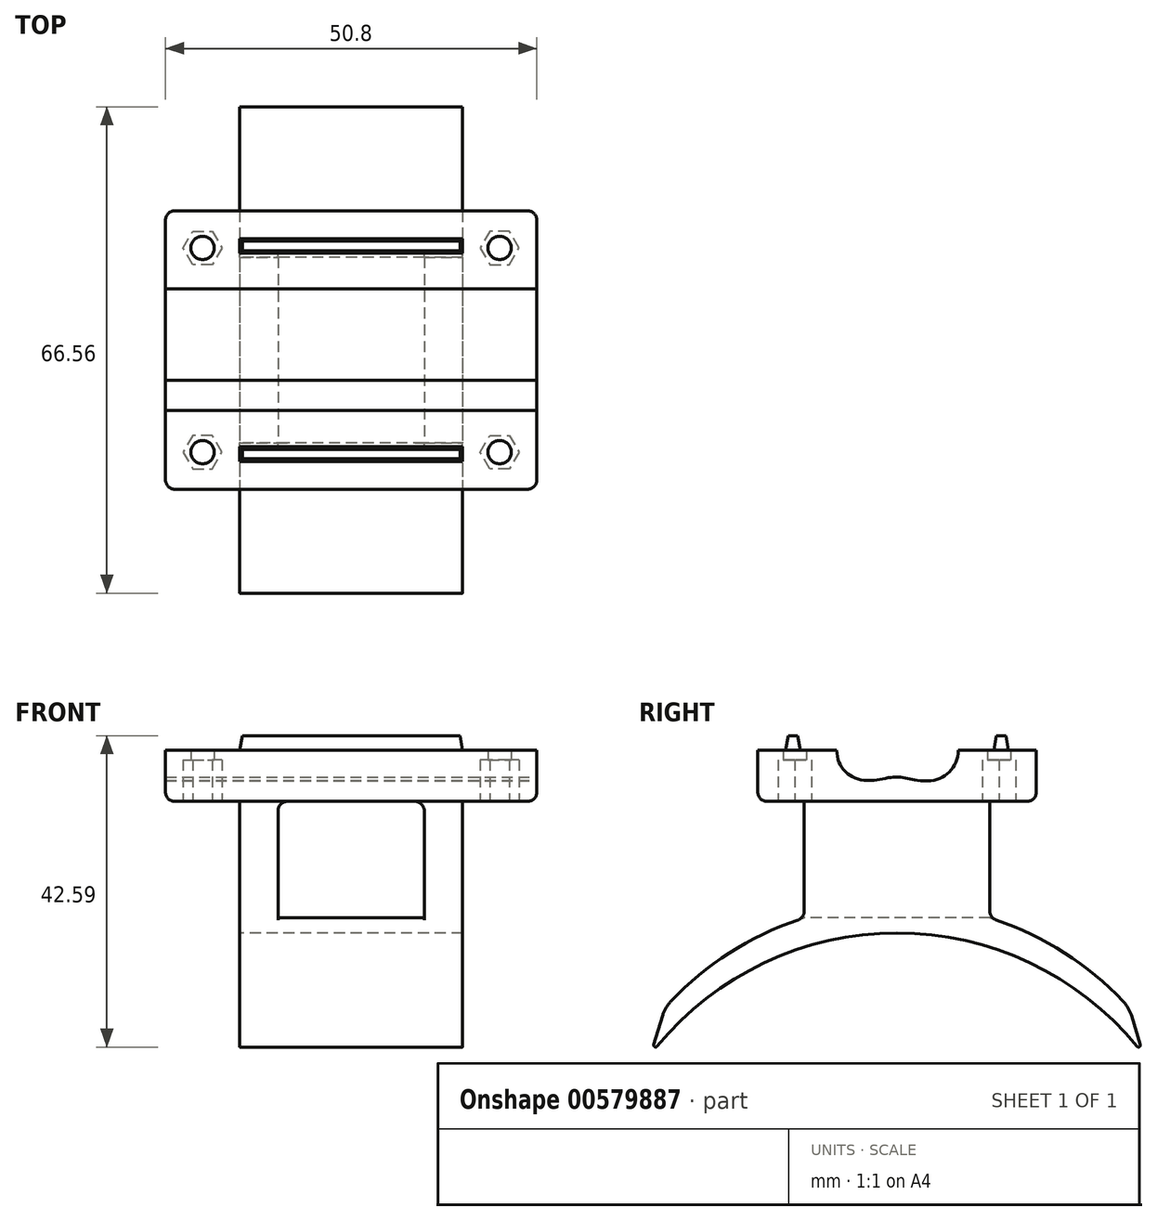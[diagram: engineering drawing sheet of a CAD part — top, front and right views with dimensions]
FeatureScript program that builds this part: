
annotation { "Feature Type Name" : "Feature", "Feature Type Description" : "" }
export const myFeature = defineFeature(function(context is Context, id is Id, definition is map)
    precondition{}
    {
        {
            var Q0;
            Q0=qCreatedBy(makeId("Top.planeOp"),FACE);
            var sketch = newSketch(context, id + "F0", { "sketchPlane" : qUnion([Q0])});
            skLineSegment(sketch, "E0.bottom", {"start": v(-38.1, 0) * mm, "end": v(38.1, 0) * mm});
            skLineSegment(sketch, "E0.top", {"start": v(-38.1, -4.13) * mm, "end": v(38.1, -4.13) * mm});
            skLineSegment(sketch, "E0.left", {"start": v(-38.1, 0) * mm, "end": v(-38.1, -4.13) * mm});
            skLineSegment(sketch, "E0.right", {"start": v(38.1, 0) * mm, "end": v(38.1, -4.13) * mm});
            skLineSegment(sketch, "E1.top", {"start": v(-38.1, 4.2) * mm, "end": v(38.1, 4.2) * mm});
            skLineSegment(sketch, "E1.left", {"start": v(-38.1, 0) * mm, "end": v(-38.1, 4.2) * mm});
            skLineSegment(sketch, "E1.right", {"start": v(38.1, 0) * mm, "end": v(38.1, 4.2) * mm});
            skLineSegment(sketch, "E2.MirrorCS", {"start": v(38.1, 8.38) * mm, "end": v(38.1, 4.2) * mm});
            skLineSegment(sketch, "E3.MirrorCS", {"start": v(-38.1, 8.38) * mm, "end": v(38.1, 8.38) * mm});
            skLineSegment(sketch, "E4.MirrorCS", {"start": v(-38.1, 8.38) * mm, "end": v(-38.1, 4.2) * mm});
            skLineSegment(sketch, "E5.MirrorCS", {"start": v(38.1, -8.25) * mm, "end": v(38.1, -4.12) * mm});
            skLineSegment(sketch, "E6.MirrorCS", {"start": v(-38.1, -8.25) * mm, "end": v(38.1, -8.25) * mm});
            skLineSegment(sketch, "E7.MirrorCS", {"start": v(-38.1, -8.25) * mm, "end": v(-38.1, -4.12) * mm});
            skSolve(sketch);
        }
        {
            var Q0;
            Q0=qCreatedBy(makeId("Top.planeOp"),FACE);
            var sketch = newSketch(context, id + "F1", { "sketchPlane" : qUnion([Q0])});
            skLineSegment(sketch, "E8.bottom", {"start": v(-25.4, 19.05) * mm, "end": v(25.4, 19.05) * mm});
            skLineSegment(sketch, "E8.top", {"start": v(-25.4, -19.05) * mm, "end": v(25.4, -19.05) * mm});
            skLineSegment(sketch, "E8.left", {"start": v(-25.4, 19.05) * mm, "end": v(-25.4, -19.05) * mm});
            skLineSegment(sketch, "E8.right", {"start": v(25.4, 19.05) * mm, "end": v(25.4, -19.05) * mm});
            skSolve(sketch);
        }
        {
            var Q0;
            Q0=qSketchRegion(id+"F1",true);
            extrude(context, id + "F2", {"entities" : qUnion([Q0]), "oppositeDirection" : true, "depth" : 7 * mm, "offsetDistance" : 25.4 * mm});
        }
        {
            var Q0;
            Q0=makeQuery(id+"F2.opExtrude","SWEPT_FACE",FACE,{"disambiguationData":[OSD([sQuery(id+"F1.wireOp",EDGE,"E8.right")])]});
            var sketch = newSketch(context, id + "F3", { "sketchPlane" : qUnion([Q0])});
            skLineSegment(sketch, "E9.0", {"start": v(-8.25, 0) * mm, "end": v(-4.12, 0) * mm});
            skLineSegment(sketch, "E10.0", {"start": v(8.38, 0) * mm, "end": v(4.2, 0) * mm});
            skArc(sketch, "E11", {"start": v(-4.13, 4.13) * mm, "mid": v(-8.25, 0) * mm, "end": v(-4.12, -4.13) * mm});
            skArc(sketch, "E12", {"start": v(4.2, -4.2) * mm, "mid": v(8.38, 0) * mm, "end": v(4.2, 4.2) * mm});
            skFitSpline(sketch, "E13", {"points": [v(-4.12, 4.13) * mm, v(0, 3.54) * mm, v(4.2, 4.2) * mm], "startDerivative": vector(10.24, -0.07) * mm, "endDerivative": vector(9.95, 0.46) * mm});
            skFitSpline(sketch, "E14", {"points": [v(-4.12, -4.13) * mm, v(0, -3.63) * mm, v(4.2, -4.2) * mm], "startDerivative": vector(7.18, -0.46) * mm, "endDerivative": vector(12.23, 0.06) * mm});
            skSolve(sketch);
        }
        {
            var Q0;
            Q0=qSketchRegion(id+"F3",true);
            var Q1;
            Q1=makeQuery(id+"F2.opExtrude","SWEPT_FACE",FACE,{"disambiguationData":[OSD([sQuery(id+"F1.wireOp",EDGE,"E8.left")])]});
            extrude(context, id + "F4", {"entities" : qUnion([Q0]), "operationType" : NewBodyOperationType.REMOVE, "endBound" : BoundingType.UP_TO_SURFACE, "oppositeDirection" : true, "depth" : 25.4 * mm, "endBoundEntityFace" : qUnion([Q1]), "offsetDistance" : 25.4 * mm});
        }
        {
            var Q0;
            Q0=qCreatedBy(makeId("Right.planeOp"),FACE);
            var sketch = newSketch(context, id + "F5", { "sketchPlane" : qUnion([Q0])});
            skArc(sketch, "E15", {"start": v(33.66, -41.53) * mm, "mid": v(0, -24.98) * mm, "end": v(-33.65, -41.53) * mm});
            skArc(sketch, "E16", {"start": v(31.75, -35.23) * mm, "mid": v(0, -20.98) * mm, "end": v(-31.75, -35.23) * mm});
            skLineSegment(sketch, "E17.0", {"start": v(19.05, -6.99) * mm, "end": v(-19.05, -6.99) * mm});
            skLineSegment(sketch, "E18", {"start": v(12.7, -22.93) * mm, "end": v(12.7, -6.99) * mm});
            skLineSegment(sketch, "E19", {"start": v(12.7, -6.99) * mm, "end": v(-12.7, -6.99) * mm});
            skLineSegment(sketch, "E20", {"start": v(-12.7, -6.99) * mm, "end": v(-12.7, -22.93) * mm});
            skLineSegment(sketch, "E21", {"start": v(-33.65, -41.53) * mm, "end": v(-31.75, -35.23) * mm});
            skLineSegment(sketch, "E22", {"start": v(31.75, -35.23) * mm, "end": v(33.66, -41.53) * mm});
            skSolve(sketch);
        }
        {
            var Q0;
            Q0=qSketchRegion(id+"F5",true);
            extrude(context, id + "F6", {"entities" : qUnion([Q0]), "operationType" : NewBodyOperationType.ADD, "depth" : 15.24 * mm, "offsetDistance" : 25.4 * mm, "hasSecondDirection" : true, "secondDirectionOppositeDirection" : true, "secondDirectionDepth" : 15.24 * mm});
        }
        {
            var Q0;
            Q0=makeQuery(id+"F6.opExtrude","SWEPT_FACE",FACE,{"disambiguationData":[OSD([sQuery(id+"F5.wireOp",EDGE,"E20")])]});
            var sketch = newSketch(context, id + "F7", { "sketchPlane" : qUnion([Q0])});
            skLineSegment(sketch, "E23.bottom", {"start": v(-10, -6.99) * mm, "end": v(10, -6.99) * mm});
            skLineSegment(sketch, "E23.top", {"start": v(-10, -22.93) * mm, "end": v(10, -22.93) * mm});
            skLineSegment(sketch, "E23.left", {"start": v(-10, -6.99) * mm, "end": v(-10, -22.93) * mm});
            skLineSegment(sketch, "E23.right", {"start": v(10, -6.98) * mm, "end": v(10, -22.93) * mm});
            skSolve(sketch);
        }
        {
            var Q0;
            Q0=qSketchRegion(id+"F7",true);
            extrude(context, id + "F8", {"entities" : qUnion([Q0]), "operationType" : NewBodyOperationType.REMOVE, "oppositeDirection" : true, "depth" : 25.4 * mm, "offsetDistance" : 25.4 * mm});
        }
        {
            var Q0;
            Q0=makeQuery(id+"F8.boolean.opBoolean","MERGE",FACE,{"derivedFrom":[makeQuery(id+"F2.opExtrude","CAP_FACE",FACE,{"disambiguationData":[OSD([sQuery(id+"F1.wireOp",EDGE,"E8.bottom"),sQuery(id+"F1.wireOp",EDGE,"E8.top"),sQuery(id+"F1.wireOp",EDGE,"E8.left"),sQuery(id+"F1.wireOp",EDGE,"E8.right")])],"isStart":false}),makeQuery(id+"F8.opExtrude","SWEPT_FACE",FACE,{"disambiguationData":[OSD([sQuery(id+"F7.wireOp",EDGE,"E23.bottom")])]})]});
            var sketch = newSketch(context, id + "F9", { "sketchPlane" : qUnion([Q0])});
            skCircle(sketch, "E24", {"center": v(20.32, -13.97) * mm, "radius": 1.6 * mm});
            skCircle(sketch, "E25.MirrorC", {"center": v(-20.32, -13.97) * mm, "radius": 1.6 * mm});
            skCircle(sketch, "E26.MirrorC", {"center": v(-20.32, 13.97) * mm, "radius": 1.6 * mm});
            skCircle(sketch, "E27.MirrorC", {"center": v(20.32, 13.97) * mm, "radius": 1.6 * mm});
            skSolve(sketch);
        }
        {
            var Q0;
            Q0=qSketchRegion(id+"F9",true);
            extrude(context, id + "F10", {"entities" : qUnion([Q0]), "operationType" : NewBodyOperationType.REMOVE, "oppositeDirection" : true, "depth" : 25.4 * mm, "offsetDistance" : 25.4 * mm});
        }
        {
            var Q0;
            Q0=makeQuery(id+"F8.boolean.opBoolean","MERGE",FACE,{"derivedFrom":[makeQuery(id+"F2.opExtrude","CAP_FACE",FACE,{"disambiguationData":[OSD([sQuery(id+"F1.wireOp",EDGE,"E8.bottom"),sQuery(id+"F1.wireOp",EDGE,"E8.top"),sQuery(id+"F1.wireOp",EDGE,"E8.left"),sQuery(id+"F1.wireOp",EDGE,"E8.right")])],"isStart":false}),makeQuery(id+"F8.opExtrude","SWEPT_FACE",FACE,{"disambiguationData":[OSD([sQuery(id+"F7.wireOp",EDGE,"E23.bottom")])]})]});
            var sketch = newSketch(context, id + "F11", { "sketchPlane" : qUnion([Q0])});
            skCircle(sketch, "E28.0", {"center": v(20.32, -13.97) * mm, "radius": 1.6 * mm});
            skCircle(sketch, "E29.cCircle", {"center": v(20.32, -13.97) * mm, "radius": 2.65 * mm, "construction": true});
            skLineSegment(sketch, "E29.0", {"start": v(22.97, -13.97) * mm, "end": v(21.64, -16.26) * mm});
            skLineSegment(sketch, "E29.1", {"start": v(21.65, -16.26) * mm, "end": v(19, -16.26) * mm});
            skLineSegment(sketch, "E29.2", {"start": v(19, -16.26) * mm, "end": v(17.67, -13.97) * mm});
            skLineSegment(sketch, "E29.3", {"start": v(17.67, -13.97) * mm, "end": v(19, -11.68) * mm});
            skLineSegment(sketch, "E29.4", {"start": v(19, -11.68) * mm, "end": v(21.65, -11.68) * mm});
            skLineSegment(sketch, "E29.5", {"start": v(21.65, -11.68) * mm, "end": v(22.97, -13.97) * mm});
            skLineSegment(sketch, "E30.MirrorCS", {"start": v(-21.65, -11.68) * mm, "end": v(-22.97, -13.97) * mm});
            skLineSegment(sketch, "E31.MirrorCS", {"start": v(-17.67, -13.97) * mm, "end": v(-19, -11.68) * mm});
            skLineSegment(sketch, "E32.MirrorCS", {"start": v(-22.97, -13.97) * mm, "end": v(-21.64, -16.26) * mm});
            skLineSegment(sketch, "E33.MirrorCS", {"start": v(-19, -16.26) * mm, "end": v(-17.67, -13.97) * mm});
            skCircle(sketch, "E34.MirrorC", {"center": v(-20.32, -13.97) * mm, "radius": 1.6 * mm});
            skLineSegment(sketch, "E35.MirrorCS", {"start": v(-19, -11.68) * mm, "end": v(-21.65, -11.68) * mm});
            skLineSegment(sketch, "E36.MirrorCS", {"start": v(-21.65, -16.26) * mm, "end": v(-19, -16.26) * mm});
            skCircle(sketch, "E37.MirrorC", {"center": v(-20.32, -13.97) * mm, "radius": 2.65 * mm, "construction": true});
            skLineSegment(sketch, "E38.MirrorCS", {"start": v(-17.67, 13.97) * mm, "end": v(-19, 11.68) * mm});
            skLineSegment(sketch, "E39.MirrorCS", {"start": v(-19, 16.26) * mm, "end": v(-17.67, 13.97) * mm});
            skLineSegment(sketch, "E40.MirrorCS", {"start": v(21.65, 11.68) * mm, "end": v(22.97, 13.97) * mm});
            skLineSegment(sketch, "E41.MirrorCS", {"start": v(-21.65, 16.26) * mm, "end": v(-19, 16.26) * mm});
            skCircle(sketch, "E42.MirrorC", {"center": v(-20.32, 13.97) * mm, "radius": 1.6 * mm});
            skLineSegment(sketch, "E43.MirrorCS", {"start": v(-22.97, 13.97) * mm, "end": v(-21.64, 16.26) * mm});
            skLineSegment(sketch, "E44.MirrorCS", {"start": v(17.67, 13.97) * mm, "end": v(19, 11.68) * mm});
            skLineSegment(sketch, "E45.MirrorCS", {"start": v(-21.65, 11.68) * mm, "end": v(-22.97, 13.97) * mm});
            skLineSegment(sketch, "E46.MirrorCS", {"start": v(-19, 11.68) * mm, "end": v(-21.65, 11.68) * mm});
            skLineSegment(sketch, "E47.MirrorCS", {"start": v(22.97, 13.97) * mm, "end": v(21.64, 16.26) * mm});
            skLineSegment(sketch, "E48.MirrorCS", {"start": v(19, 16.26) * mm, "end": v(17.67, 13.97) * mm});
            skLineSegment(sketch, "E49.MirrorCS", {"start": v(21.65, 16.26) * mm, "end": v(19, 16.26) * mm});
            skLineSegment(sketch, "E50.MirrorCS", {"start": v(19, 11.68) * mm, "end": v(21.65, 11.68) * mm});
            skCircle(sketch, "E51.MirrorC", {"center": v(20.32, 13.97) * mm, "radius": 2.65 * mm, "construction": true});
            skCircle(sketch, "E52.MirrorC", {"center": v(20.32, 13.97) * mm, "radius": 1.6 * mm});
            skCircle(sketch, "E53.MirrorC", {"center": v(-20.32, 13.97) * mm, "radius": 2.65 * mm, "construction": true});
            skSolve(sketch);
        }
        {
            var Q0;
            Q0=qSketchRegion(id+"F11",true);
            extrude(context, id + "F12", {"entities" : qUnion([Q0]), "operationType" : NewBodyOperationType.REMOVE, "oppositeDirection" : true, "depth" : 5.7 * mm, "offsetDistance" : 25.4 * mm});
        }
        {
            var Q0;
            {var subQ0=sQuery(id+"F1.wireOp",EDGE,"E8.bottom");var subQ1=sQuery(id+"F1.wireOp",EDGE,"E8.right");var subQ2=sQuery(id+"F1.wireOp",EDGE,"E8.left");Q0=makeQuery(id+"F4.boolean.opBoolean","SPLIT",FACE,{"disambiguationData":[TD([makeQuery(id+"F2.opExtrude","SWEPT_FACE",FACE,{"disambiguationData":[OSD([subQ0])]})])],"derivedFrom":makeQuery(id+"F2.opExtrude","CAP_FACE",FACE,{"disambiguationData":[OSD([subQ0,sQuery(id+"F1.wireOp",EDGE,"E8.top"),subQ2,subQ1])],"isStart":true})});}
            var sketch = newSketch(context, id + "F13", { "sketchPlane" : qUnion([Q0])});
            skLineSegment(sketch, "E54.bottom", {"start": v(-15.24, 15.24) * mm, "end": v(15.24, 15.24) * mm});
            skLineSegment(sketch, "E54.top", {"start": v(-15.24, 13.24) * mm, "end": v(15.24, 13.24) * mm});
            skLineSegment(sketch, "E54.left", {"start": v(-15.24, 15.24) * mm, "end": v(-15.24, 13.24) * mm});
            skLineSegment(sketch, "E54.right", {"start": v(15.24, 15.24) * mm, "end": v(15.24, 13.24) * mm});
            skLineSegment(sketch, "E55.MirrorCS", {"start": v(-15.24, -15.24) * mm, "end": v(-15.24, -13.24) * mm});
            skLineSegment(sketch, "E56.MirrorCS", {"start": v(15.24, -15.24) * mm, "end": v(15.24, -13.24) * mm});
            skLineSegment(sketch, "E57.MirrorCS", {"start": v(-15.24, -15.24) * mm, "end": v(15.24, -15.24) * mm});
            skLineSegment(sketch, "E58.MirrorCS", {"start": v(-15.24, -13.24) * mm, "end": v(15.24, -13.24) * mm});
            skSolve(sketch);
        }
        {
            var Q0;
            Q0=qSketchRegion(id+"F13",true);
            extrude(context, id + "F14", {"entities" : qUnion([Q0]), "operationType" : NewBodyOperationType.ADD, "depth" : 2 * mm, "offsetDistance" : 25.4 * mm, "hasDraft" : true, "draftAngle" : 10 * degree, "draftPullDirection" : true});
        }
        {
            var Q0;
            Q0=makeQuery(id+"F6.opExtrude","SWEPT_EDGE",EDGE,{"disambiguationData":[OSD([sQuery(id+"F5.wireOp",EDGE,"E15"),sQuery(id+"F5.wireOp",EDGE,"E22")])]});
            var Q1;
            Q1=makeQuery(id+"F6.opExtrude","SWEPT_EDGE",EDGE,{"disambiguationData":[OSD([sQuery(id+"F5.wireOp",EDGE,"E15"),sQuery(id+"F5.wireOp",EDGE,"E21")])]});
            fillet(context, id + "F15", {"entities" : qUnion([Q0, Q1]), "radius" : 0.25 * mm, "tangentPropagation" : true, "allowEdgeOverflow" : false});
        }
        {
            var Q0;
            Q0=makeQuery(id+"F6.opExtrude","SWEPT_EDGE",EDGE,{"disambiguationData":[OSD([sQuery(id+"F5.wireOp",EDGE,"E16"),sQuery(id+"F5.wireOp",EDGE,"E22")])]});
            var Q1;
            Q1=makeQuery(id+"F6.opExtrude","SWEPT_EDGE",EDGE,{"disambiguationData":[OSD([sQuery(id+"F5.wireOp",EDGE,"E16"),sQuery(id+"F5.wireOp",EDGE,"E21")])]});
            fillet(context, id + "F16", {"entities" : qUnion([Q0, Q1]), "radius" : 5.08 * mm, "tangentPropagation" : true, "allowEdgeOverflow" : false});
        }
        {
            var Q0;
            {var subQ1=sQuery(id+"F5.wireOp",EDGE,"E16");var subQ2=sQuery(id+"F5.wireOp",EDGE,"E20");Q0=makeQuery(id+"F8.boolean.opBoolean","SPLIT",EDGE,{"disambiguationData":[TD([makeQuery(id+"F8.opExtrude","SWEPT_FACE",FACE,{"disambiguationData":[OSD([sQuery(id+"F7.wireOp",EDGE,"E23.right")])]})])],"derivedFrom":makeQuery(id+"F6.opExtrude","SWEPT_EDGE",EDGE,{"disambiguationData":[OSD([subQ1,subQ2])]})});}
            var Q1;
            {var subQ0=sQuery(id+"F5.wireOp",EDGE,"E20");var subQ2=sQuery(id+"F5.wireOp",EDGE,"E16");Q1=makeQuery(id+"F8.boolean.opBoolean","SPLIT",EDGE,{"disambiguationData":[TD([makeQuery(id+"F8.opExtrude","SWEPT_FACE",FACE,{"disambiguationData":[OSD([sQuery(id+"F7.wireOp",EDGE,"E23.left")])]})])],"derivedFrom":makeQuery(id+"F6.opExtrude","SWEPT_EDGE",EDGE,{"disambiguationData":[OSD([subQ2,subQ0])]})});}
            var Q2;
            {var subQ0=sQuery(id+"F5.wireOp",EDGE,"E18");var subQ1=makeQuery(id+"F6.opExtrude","SWEPT_FACE",FACE,{"disambiguationData":[OSD([subQ0])]});var subQ2=sQuery(id+"F5.wireOp",EDGE,"E22");var subQ3=sQuery(id+"F5.wireOp",EDGE,"E16");var subQ4=makeQuery(id+"F6.opExtrude","SWEPT_FACE",FACE,{"disambiguationData":[OSD([subQ3]),TDD([makeQuery(id+"F5.imprint","IMPRINT",EDGE,{"disambiguationData":[TD([[makeQuery(id+"F5.imprint","INTERSECT",VERTEX,{"derivedFrom":[subQ3,subQ2]}),-1.0]])],"derivedFrom":subQ3})])]});Q2=makeQuery(id+"F8.boolean.opBoolean","SPLIT",EDGE,{"disambiguationData":[topologyDisambiguationEdgeConnected([subQ4,subQ1]),TD([makeQuery(id+"F8.opExtrude","SWEPT_FACE",FACE,{"disambiguationData":[OSD([sQuery(id+"F7.wireOp",EDGE,"E23.right")])]})])],"derivedFrom":makeQuery(id+"F6.opExtrude","SWEPT_EDGE",EDGE,{"disambiguationData":[OSD([subQ3,subQ0])]})});}
            var Q3;
            {var subQ0=sQuery(id+"F5.wireOp",EDGE,"E18");var subQ1=makeQuery(id+"F6.opExtrude","SWEPT_FACE",FACE,{"disambiguationData":[OSD([subQ0])]});var subQ2=sQuery(id+"F5.wireOp",EDGE,"E22");var subQ3=sQuery(id+"F5.wireOp",EDGE,"E16");var subQ4=makeQuery(id+"F6.opExtrude","SWEPT_FACE",FACE,{"disambiguationData":[OSD([subQ3]),TDD([makeQuery(id+"F5.imprint","IMPRINT",EDGE,{"disambiguationData":[TD([[makeQuery(id+"F5.imprint","INTERSECT",VERTEX,{"derivedFrom":[subQ3,subQ2]}),-1.0]])],"derivedFrom":subQ3})])]});Q3=makeQuery(id+"F8.boolean.opBoolean","SPLIT",EDGE,{"disambiguationData":[topologyDisambiguationEdgeConnected([subQ4,subQ1]),TD([makeQuery(id+"F8.opExtrude","SWEPT_FACE",FACE,{"disambiguationData":[OSD([sQuery(id+"F7.wireOp",EDGE,"E23.left")])]})])],"derivedFrom":makeQuery(id+"F6.opExtrude","SWEPT_EDGE",EDGE,{"disambiguationData":[OSD([subQ3,subQ0])]})});}
            fillet(context, id + "F17", {"entities" : qUnion([Q0, Q1, Q2, Q3]), "radius" : 1.27 * mm, "tangentPropagation" : true, "allowEdgeOverflow" : false});
        }
        {
            var Q0;
            {var subQ0=sQuery(id+"F5.wireOp",EDGE,"E18");var subQ1=sQuery(id+"F5.wireOp",EDGE,"E19");Q0=makeQuery(id+"F8.boolean.opBoolean","SPLIT",EDGE,{"disambiguationData":[TD([makeQuery(id+"F8.opExtrude","SWEPT_FACE",FACE,{"disambiguationData":[OSD([sQuery(id+"F7.wireOp",EDGE,"E23.right")])]})])],"derivedFrom":makeQuery(id+"F6.opExtrude","SWEPT_EDGE",EDGE,{"disambiguationData":[OSD([subQ0,subQ1])]})});}
            var Q1;
            Q1=makeQuery(id+"F6.opExtrude","CAP_EDGE",EDGE,{"disambiguationData":[OSD([sQuery(id+"F5.wireOp",EDGE,"E19")])],"isStart":false});
            var Q2;
            {var subQ0=sQuery(id+"F5.wireOp",EDGE,"E20");var subQ1=sQuery(id+"F5.wireOp",EDGE,"E19");Q2=makeQuery(id+"F8.boolean.opBoolean","SPLIT",EDGE,{"disambiguationData":[TD([makeQuery(id+"F8.opExtrude","SWEPT_FACE",FACE,{"disambiguationData":[OSD([sQuery(id+"F7.wireOp",EDGE,"E23.right")])]})])],"derivedFrom":makeQuery(id+"F6.opExtrude","SWEPT_EDGE",EDGE,{"disambiguationData":[OSD([subQ1,subQ0])]})});}
            var Q3;
            Q3=makeQuery(id+"F8.boolean.opBoolean","COPY",EDGE,{"derivedFrom":makeQuery(id+"F8.opExtrude","SWEPT_EDGE",EDGE,{"disambiguationData":[OSD([sQuery(id+"F5.wireOp",EDGE,"E19"),sQuery(id+"F5.wireOp",EDGE,"E20"),sQuery(id+"F7.wireOp",EDGE,"E23.bottom"),sQuery(id+"F7.wireOp",EDGE,"E23.right")])]})});
            var Q4;
            {var subQ0=sQuery(id+"F5.wireOp",EDGE,"E20");var subQ1=sQuery(id+"F5.wireOp",EDGE,"E19");Q4=makeQuery(id+"F8.boolean.opBoolean","SPLIT",EDGE,{"disambiguationData":[TD([makeQuery(id+"F8.opExtrude","SWEPT_FACE",FACE,{"disambiguationData":[OSD([sQuery(id+"F7.wireOp",EDGE,"E23.left")])]})])],"derivedFrom":makeQuery(id+"F6.opExtrude","SWEPT_EDGE",EDGE,{"disambiguationData":[OSD([subQ1,subQ0])]})});}
            var Q5;
            Q5=makeQuery(id+"F6.opExtrude","CAP_EDGE",EDGE,{"disambiguationData":[OSD([sQuery(id+"F5.wireOp",EDGE,"E19")])],"isStart":true});
            var Q6;
            Q6=makeQuery(id+"F8.boolean.opBoolean","COPY",EDGE,{"derivedFrom":makeQuery(id+"F8.opExtrude","SWEPT_EDGE",EDGE,{"disambiguationData":[OSD([sQuery(id+"F5.wireOp",EDGE,"E19"),sQuery(id+"F5.wireOp",EDGE,"E20"),sQuery(id+"F7.wireOp",EDGE,"E23.bottom"),sQuery(id+"F7.wireOp",EDGE,"E23.left")])]})});
            var Q7;
            {var subQ0=sQuery(id+"F5.wireOp",EDGE,"E18");var subQ1=sQuery(id+"F5.wireOp",EDGE,"E19");Q7=makeQuery(id+"F8.boolean.opBoolean","SPLIT",EDGE,{"disambiguationData":[TD([makeQuery(id+"F8.opExtrude","SWEPT_FACE",FACE,{"disambiguationData":[OSD([sQuery(id+"F7.wireOp",EDGE,"E23.left")])]})])],"derivedFrom":makeQuery(id+"F6.opExtrude","SWEPT_EDGE",EDGE,{"disambiguationData":[OSD([subQ0,subQ1])]})});}
            fillet(context, id + "F18", {"entities" : qUnion([Q0, Q1, Q2, Q3, Q4, Q5, Q6, Q7]), "radius" : 1.27 * mm, "tangentPropagation" : true, "allowEdgeOverflow" : false});
        }
        {
            var Q0;
            Q0=makeQuery(id+"F2.opExtrude","SWEPT_EDGE",EDGE,{"disambiguationData":[OSD([sQuery(id+"F1.wireOp",EDGE,"E8.top"),sQuery(id+"F1.wireOp",EDGE,"E8.left")])]});
            var Q1;
            Q1=makeQuery(id+"F2.opExtrude","CAP_EDGE",EDGE,{"disambiguationData":[OSD([sQuery(id+"F1.wireOp",EDGE,"E8.left")])],"isStart":false});
            var Q2;
            Q2=makeQuery(id+"F2.opExtrude","CAP_EDGE",EDGE,{"disambiguationData":[OSD([sQuery(id+"F1.wireOp",EDGE,"E8.top")])],"isStart":false});
            var Q3;
            Q3=makeQuery(id+"F2.opExtrude","SWEPT_EDGE",EDGE,{"disambiguationData":[OSD([sQuery(id+"F1.wireOp",EDGE,"E8.top"),sQuery(id+"F1.wireOp",EDGE,"E8.right")])]});
            var Q4;
            Q4=makeQuery(id+"F2.opExtrude","CAP_EDGE",EDGE,{"disambiguationData":[OSD([sQuery(id+"F1.wireOp",EDGE,"E8.right")])],"isStart":false});
            var Q5;
            Q5=makeQuery(id+"F2.opExtrude","SWEPT_EDGE",EDGE,{"disambiguationData":[OSD([sQuery(id+"F1.wireOp",EDGE,"E8.bottom"),sQuery(id+"F1.wireOp",EDGE,"E8.right")])]});
            var Q6;
            Q6=makeQuery(id+"F2.opExtrude","CAP_EDGE",EDGE,{"disambiguationData":[OSD([sQuery(id+"F1.wireOp",EDGE,"E8.bottom")])],"isStart":false});
            var Q7;
            Q7=makeQuery(id+"F2.opExtrude","SWEPT_EDGE",EDGE,{"disambiguationData":[OSD([sQuery(id+"F1.wireOp",EDGE,"E8.bottom"),sQuery(id+"F1.wireOp",EDGE,"E8.left")])]});
            fillet(context, id + "F19", {"entities" : qUnion([Q0, Q1, Q2, Q3, Q4, Q5, Q6, Q7]), "radius" : 1.27 * mm, "tangentPropagation" : true, "allowEdgeOverflow" : false});
        }
    });
